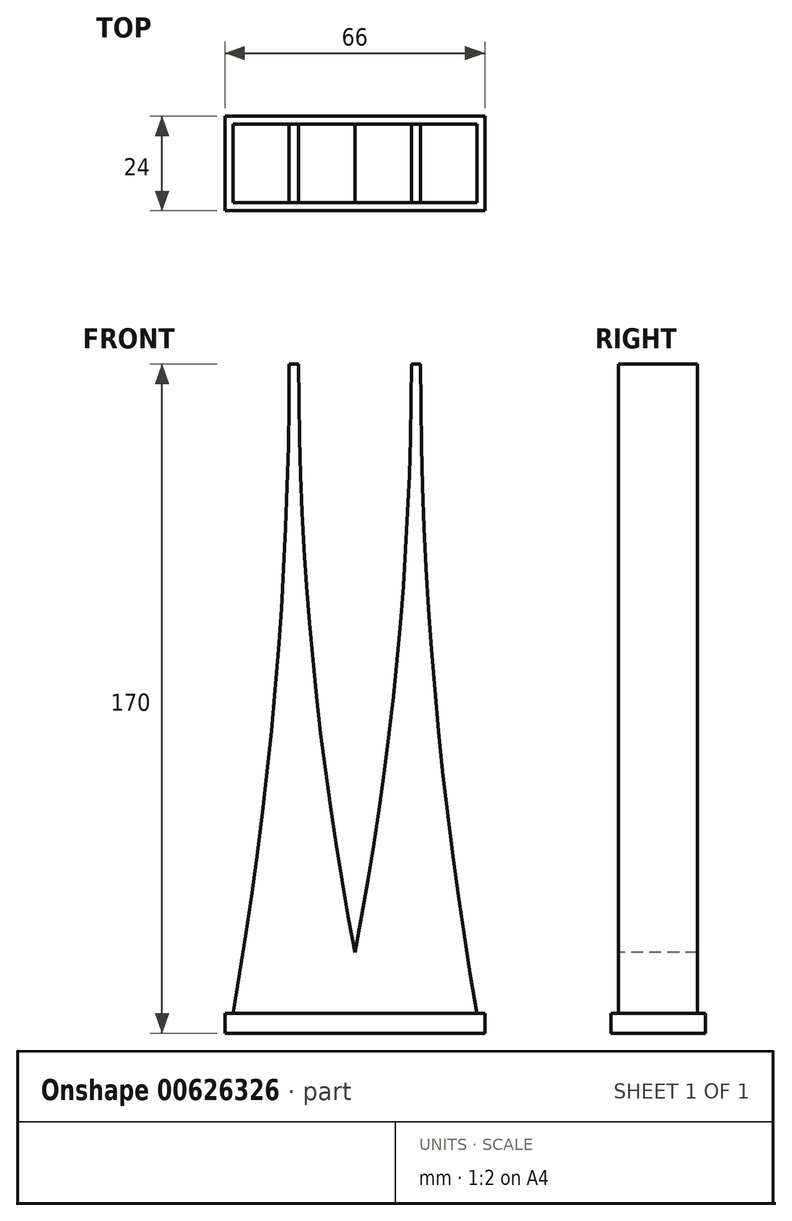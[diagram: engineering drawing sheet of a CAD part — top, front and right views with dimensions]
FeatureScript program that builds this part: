
annotation { "Feature Type Name" : "Feature", "Feature Type Description" : "" }
export const myFeature = defineFeature(function(context is Context, id is Id, definition is map)
    precondition{}
    {
        {
            var Q0;
            Q0=qCreatedBy(makeId("Front.planeOp"),FACE);
            var sketch = newSketch(context, id + "F0", { "sketchPlane" : qUnion([Q0])});
            skLineSegment(sketch, "E0", {"start": v(0, 0) * mm, "end": v(15.5, 0) * mm});
            skLineSegment(sketch, "E1", {"start": v(15.5, 0) * mm, "end": v(15.5, 175) * mm});
            skLineSegment(sketch, "E2", {"start": v(15.5, 175) * mm, "end": v(14.3, 175) * mm});
            skLineSegment(sketch, "E3", {"start": v(14.3, 175) * mm, "end": v(14.3, 165) * mm});
            skLineSegment(sketch, "E4", {"start": v(14.3, 165) * mm, "end": v(16.7, 165) * mm});
            skLineSegment(sketch, "E5", {"start": v(16.7, 165) * mm, "end": v(16.7, 175) * mm});
            skLineSegment(sketch, "E6", {"start": v(16.7, 175) * mm, "end": v(15.5, 175) * mm});
            skLineSegment(sketch, "E7", {"start": v(0, 0) * mm, "end": v(0, 15.5) * mm});
            skArc(sketch, "E8", {"start": v(14.3, 165) * mm, "mid": v(10.72, 89.9) * mm, "end": v(0, 15.5) * mm});
            skLineSegment(sketch, "E9", {"start": v(15.5, 0) * mm, "end": v(31, 0) * mm});
            skArc(sketch, "E10.MirrorCS", {"start": v(-14.3, 165) * mm, "mid": v(-10.72, 89.9) * mm, "end": v(0, 15.5) * mm});
            skLineSegment(sketch, "E11.MirrorCS", {"start": v(-15.5, 0) * mm, "end": v(-15.5, 175) * mm});
            skLineSegment(sketch, "E12.MirrorCS", {"start": v(-15.5, 0) * mm, "end": v(-31, 0) * mm});
            skLineSegment(sketch, "E13.MirrorCS", {"start": v(0, 0) * mm, "end": v(-15.5, 0) * mm});
            skLineSegment(sketch, "E14.MirrorCS", {"start": v(-14.3, 165) * mm, "end": v(-16.7, 165) * mm});
            skLineSegment(sketch, "E15.MirrorCS", {"start": v(-16.7, 165) * mm, "end": v(-16.7, 175) * mm});
            skLineSegment(sketch, "E16.MirrorCS", {"start": v(-16.7, 175) * mm, "end": v(-15.5, 175) * mm});
            skLineSegment(sketch, "E17.MirrorCS", {"start": v(-15.5, 175) * mm, "end": v(-14.3, 175) * mm});
            skLineSegment(sketch, "E18.MirrorCS", {"start": v(-14.3, 175) * mm, "end": v(-14.3, 165) * mm});
            skArc(sketch, "E19", {"start": v(16.7, 165) * mm, "mid": v(20.28, 82.2) * mm, "end": v(31, 0) * mm});
            skArc(sketch, "E20.MirrorCS", {"start": v(-16.7, 165) * mm, "mid": v(-20.28, 82.2) * mm, "end": v(-31, 0) * mm});
            skSolve(sketch);
        }
        {
            var Q0;
            {var subQ0=sQuery(id+"F0.wireOp",EDGE,"E12.MirrorCS");Q0=makeQuery(id+"F0.imprint","IMPRINT",FACE,{"disambiguationData":[TD([[makeQuery(id+"F0.imprint","IMPRINT",EDGE,{"derivedFrom":subQ0}),-1.0]])]});}
            var Q1;
            Q1=makeQuery(id+"F0.imprint","IMPRINT",FACE,{"disambiguationData":[TD([[makeQuery(id+"F0.imprint","IMPRINT",EDGE,{"derivedFrom":sQuery(id+"F0.wireOp",EDGE,"E7")}),1.0]])]});
            var Q2;
            {var subQ1=sQuery(id+"F0.wireOp",EDGE,"E0");Q2=makeQuery(id+"F0.imprint","IMPRINT",FACE,{"disambiguationData":[TD([[makeQuery(id+"F0.imprint","IMPRINT",EDGE,{"derivedFrom":subQ1}),1.0]])]});}
            var Q3;
            {var subQ0=sQuery(id+"F0.wireOp",EDGE,"E9");Q3=makeQuery(id+"F0.imprint","IMPRINT",FACE,{"disambiguationData":[TD([[makeQuery(id+"F0.imprint","IMPRINT",EDGE,{"derivedFrom":subQ0}),1.0]])]});}
            extrude(context, id + "F1", {"entities" : qUnion([Q0, Q1, Q2, Q3]), "oppositeDirection" : true, "depth" : 20 * mm, "offsetDistance" : 25 * mm});
        }
        {
            var Q0;
            Q0=qCreatedBy(makeId("Top.planeOp"),FACE);
            var sketch = newSketch(context, id + "F2", { "sketchPlane" : qUnion([Q0])});
            skPoint(sketch, "E21.0", {"position": v(-31, 0) * mm});
            skPoint(sketch, "E22.0", {"position": v(31, 20) * mm});
            skLineSegment(sketch, "E23.bottom", {"start": v(-31, 0) * mm, "end": v(31, 0) * mm});
            skLineSegment(sketch, "E23.top", {"start": v(-31, 20) * mm, "end": v(31, 20) * mm});
            skLineSegment(sketch, "E23.left", {"start": v(-31, 0) * mm, "end": v(-31, 20) * mm});
            skLineSegment(sketch, "E23.right", {"start": v(31, 0) * mm, "end": v(31, 20) * mm});
            skLineSegment(sketch, "E24.0", {"start": v(-33, -2) * mm, "end": v(33, -2) * mm});
            skLineSegment(sketch, "E24.1", {"start": v(-33, -2) * mm, "end": v(-33, 22) * mm});
            skLineSegment(sketch, "E24.2", {"start": v(-33, 22) * mm, "end": v(33, 22) * mm});
            skLineSegment(sketch, "E24.3", {"start": v(33, -2) * mm, "end": v(33, 22) * mm});
            skSolve(sketch);
        }
        {
            var Q0;
            Q0 = qSketchRegion(id + "F2", true);
            var Q1;
            Q1=makeQuery(id+"F2.imprint","IMPRINT",FACE,{"disambiguationData":[TD([[makeQuery(id+"F2.imprint","IMPRINT",EDGE,{"derivedFrom":sQuery(id+"F2.wireOp",EDGE,"E23.bottom")}),1.0]])]});
            extrude(context, id + "F3", {"entities" : qUnion([Q0, Q1]), "operationType" : NewBodyOperationType.ADD, "oppositeDirection" : true, "depth" : 5 * mm, "offsetDistance" : 25 * mm});
        }
    });
